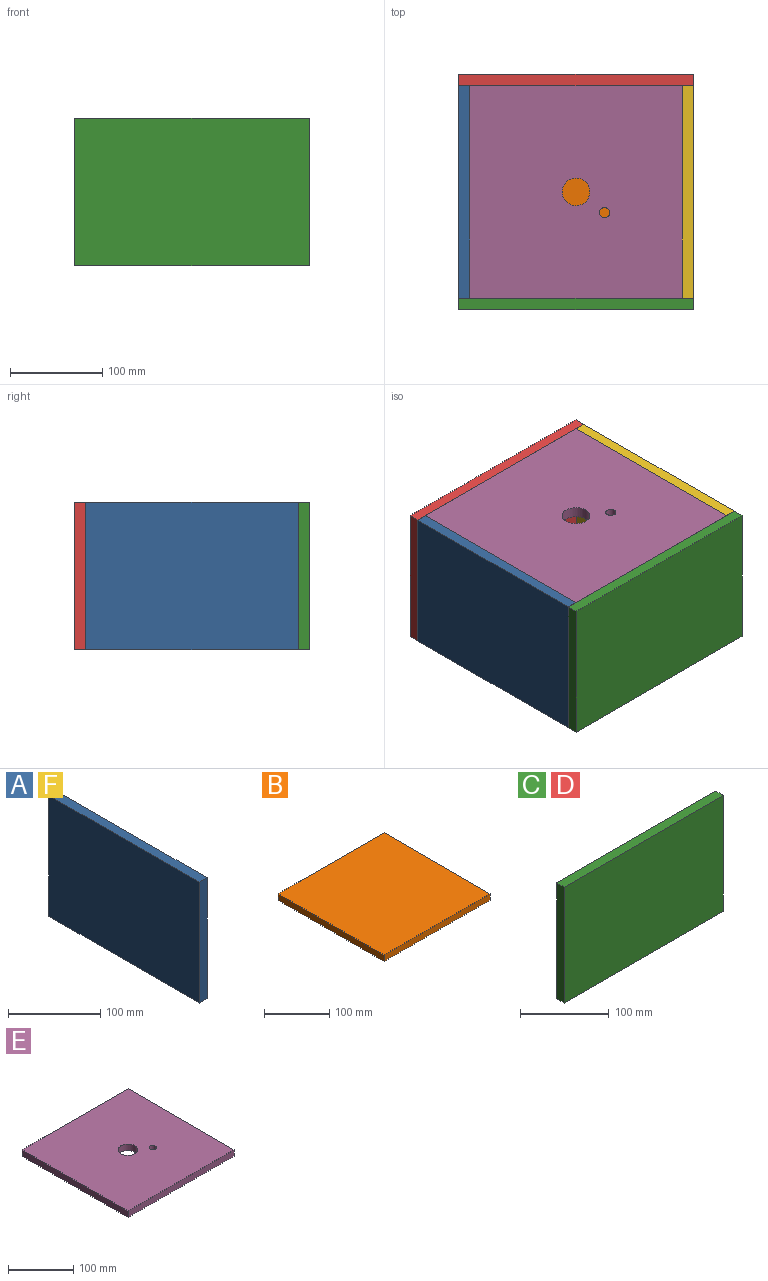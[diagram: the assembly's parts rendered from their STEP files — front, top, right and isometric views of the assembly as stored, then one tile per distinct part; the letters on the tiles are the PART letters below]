
ASSEMBLY  parts=6 mates=15
PART A: 6 faces, bbox 12x230x160 mm
  f0: plane 230x12mm, normal (0,0,-1), area 2760mm2, adj f1,f3,f4,f5
  f1: plane 160x12mm, normal (0,-1,0), area 1920mm2, adj f0,f2,f4,f5
  f2: plane 230x12mm, normal (0,0,1), area 2760mm2, adj f1,f3,f4,f5
  f3: plane 160x12mm, normal (0,1,0), area 1920mm2, adj f0,f2,f4,f5
  f4: plane 230x160mm, normal (-1,0,0), area 36800mm2, adj f0,f1,f2,f3
  f5: plane 230x160mm, normal (1,0,0), area 36800mm2, adj f0,f1,f2,f3
PART B: 6 faces, bbox 230x230x12 mm
  f0: plane 230x12mm, normal (-1,0,0), area 2760mm2, adj f1,f3,f4,f5
  f1: plane 230x12mm, normal (0,-1,0), area 2760mm2, adj f0,f2,f4,f5
  f2: plane 230x12mm, normal (1,0,0), area 2760mm2, adj f1,f3,f4,f5
  f3: plane 230x12mm, normal (0,1,0), area 2760mm2, adj f0,f2,f4,f5
  f4: plane 230x230mm, normal (0,0,1), area 52900mm2, adj f0,f1,f2,f3
  f5: plane 230x230mm, normal (0,0,-1), area 52900mm2, adj f0,f1,f2,f3
PART C: 6 faces, bbox 254x12x160 mm
  f0: plane 254x12mm, normal (0,0,-1), area 3048mm2, adj f1,f3,f4,f5
  f1: plane 160x12mm, normal (1,0,0), area 1920mm2, adj f0,f2,f4,f5
  f2: plane 254x12mm, normal (0,0,1), area 3048mm2, adj f1,f3,f4,f5
  f3: plane 160x12mm, normal (-1,0,0), area 1920mm2, adj f0,f2,f4,f5
  f4: plane 254x160mm, normal (0,-1,0), area 40640mm2, adj f0,f1,f2,f3
  f5: plane 254x160mm, normal (0,1,0), area 40640mm2, adj f0,f1,f2,f3
PART D: same geometry as C
PART E: 8 faces, bbox 230x230x12 mm
  f0: plane 230x12mm, normal (-1,0,0), area 2760mm2, adj f1,f3,f4,f5
  f1: plane 230x12mm, normal (0,-1,0), area 2760mm2, adj f0,f2,f4,f5
  f2: plane 230x12mm, normal (1,0,0), area 2760mm2, adj f1,f3,f4,f5
  f3: plane 230x12mm, normal (0,1,0), area 2760mm2, adj f0,f2,f4,f5
  f4: plane 230x230mm, normal (0,0,1), area 52098.1mm2, adj f0,f1,f2,f3,f6,f7
  f5: plane 230x230mm, normal (0,0,-1), area 52098.1mm2, adj f0,f1,f2,f3,f6,f7
  f6: cylinder r=15mm len=30mm, axis (0,0,1), area 1131mm2, adj f4,f5
  f7: cylinder r=5.5mm len=12mm, axis (0,0,1), area 414.7mm2, adj f4,f5
PART F: same geometry as A
PLACE A rot(axis=(0,1,0),180deg) t=(1.17,-27,27.01)mm
PLACE B t=(13.17,-27,-132.99)mm
PLACE C t=(1.17,-27,-132.99)mm
PLACE D t=(1.17,215,-132.99)mm
PLACE E t=(13.17,-27,15.01)mm fixed
PLACE F rot(axis=(0,1,0),180deg) t=(243.17,-27,27.01)mm
MATE planar D.f4 <-> E.f3  axis (0,-1,0) through (128.17,203,-52.99)mm
MATE planar E.f4 <-> D.f2  axis (0,0,1) through (128.12,88.05,27.01)mm
MATE planar A.f1 <-> E.f1  axis (0,-1,0) through (7.17,-27,-52.99)mm
MATE planar F.f1 <-> E.f1  axis (0,-1,0) through (249.17,-27,-52.99)mm
MATE planar E.f4 <-> A.f0  axis (0,0,1) through (128.12,88.05,27.01)mm
MATE planar E.f4 <-> C.f2  axis (0,0,1) through (128.12,88.05,27.01)mm
MATE planar B.f1 <-> A.f1  axis (0,-1,0) through (128.17,-27,-126.99)mm
MATE planar A.f5 <-> C.f3  axis (-1,0,0) through (1.17,88,-52.99)mm
MATE planar E.f4 <-> F.f0  axis (0,0,1) through (128.12,88.05,27.01)mm
MATE planar C.f5 <-> E.f1  axis (0,1,0) through (128.17,-27,-52.99)mm
MATE planar A.f5 <-> D.f3  axis (-1,0,0) through (1.17,88,-52.99)mm
MATE planar F.f5 <-> E.f2  axis (-1,0,0) through (243.17,88,-52.99)mm
MATE planar A.f4 <-> E.f0  axis (1,0,0) through (13.17,88,-52.99)mm
MATE planar B.f5 <-> A.f2  axis (0,0,-1) through (128.17,88,-132.99)mm
MATE planar A.f4 <-> B.f0  axis (1,0,0) through (13.17,88,-52.99)mm
